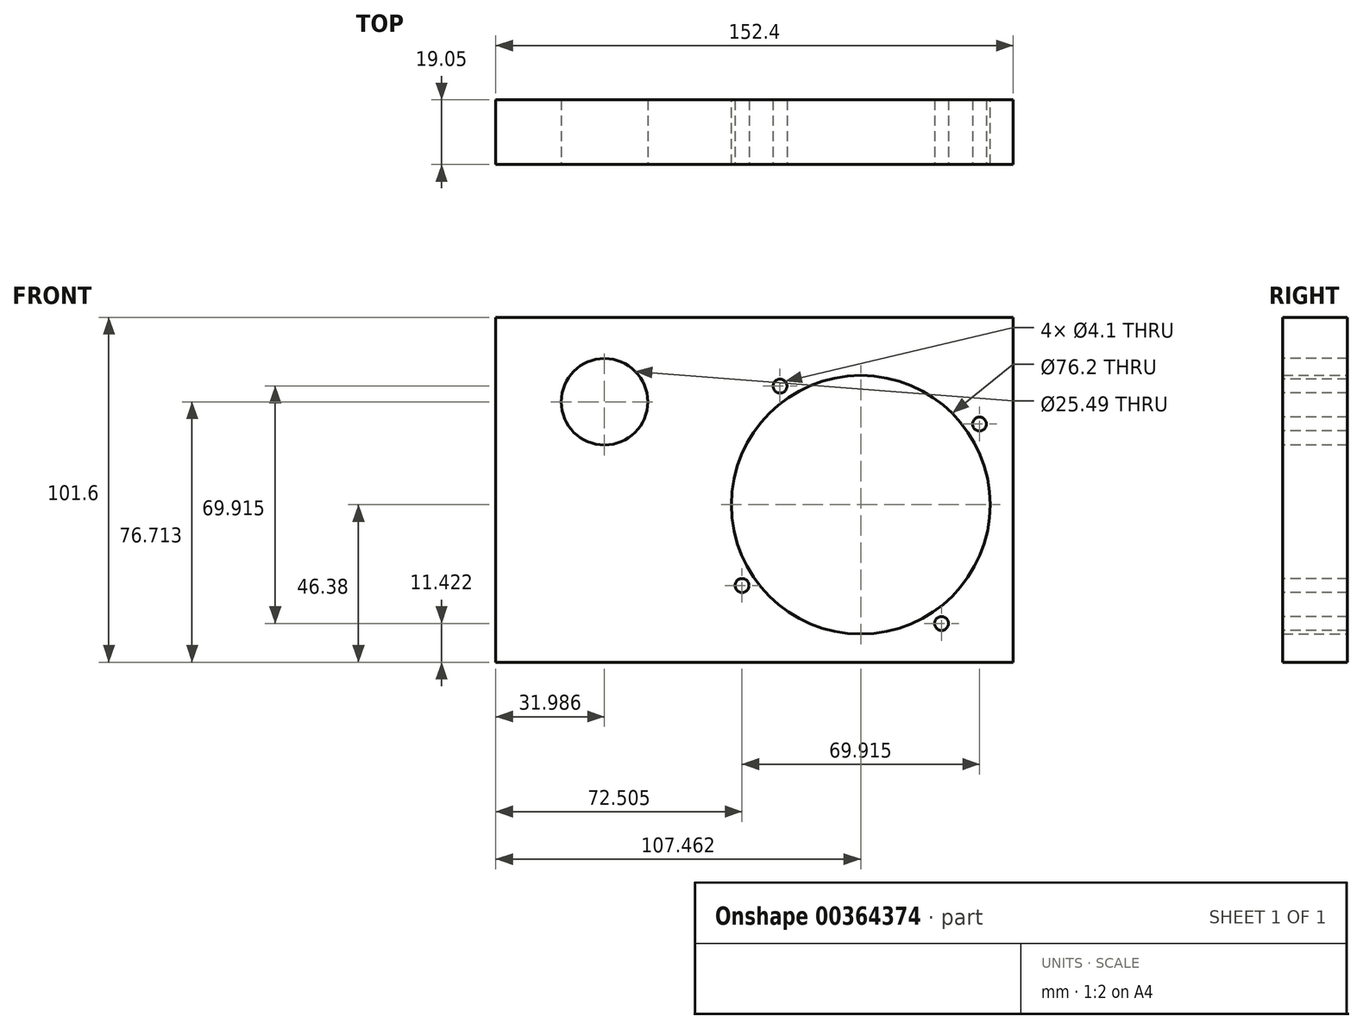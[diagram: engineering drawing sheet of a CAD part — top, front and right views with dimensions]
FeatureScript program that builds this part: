
annotation { "Feature Type Name" : "Feature", "Feature Type Description" : "" }
export const myFeature = defineFeature(function(context is Context, id is Id, definition is map)
    precondition{}
    {
        {
            var Q0;
            Q0=qCreatedBy(makeId("Front.planeOp"),FACE);
            var sketch = newSketch(context, id + "F0", { "sketchPlane" : qUnion([Q0])});
            skLineSegment(sketch, "E0.bottom", {"start": v(-73.83, 39.08) * mm, "end": v(78.57, 39.08) * mm});
            skLineSegment(sketch, "E0.top", {"start": v(-73.83, -62.52) * mm, "end": v(78.57, -62.52) * mm});
            skLineSegment(sketch, "E0.left", {"start": v(-73.83, 39.08) * mm, "end": v(-73.83, -62.52) * mm});
            skLineSegment(sketch, "E0.right", {"start": v(78.57, 39.08) * mm, "end": v(78.57, -62.52) * mm});
            skCircle(sketch, "E1", {"center": v(33.63, -16.14) * mm, "radius": 38.1 * mm});
            skSolve(sketch);
        }
        {
            var Q0;
            Q0 = qSketchRegion(id + "F0", true);
            extrude(context, id + "F1", {"entities" : qUnion([Q0]), "depth" : 19.05 * mm});
        }
        {
            var Q0;
            Q0=makeQuery(id+"F1.opExtrude","CAP_FACE",FACE,{"disambiguationData":[OSD([sQuery(id+"F0.wireOp",EDGE,"E0.bottom"),sQuery(id+"F0.wireOp",EDGE,"E0.top"),sQuery(id+"F0.wireOp",EDGE,"E0.left"),sQuery(id+"F0.wireOp",EDGE,"E0.right"),sQuery(id+"F0.wireOp",EDGE,"E1")])],"isStart":false});
            var sketch = newSketch(context, id + "F2", { "sketchPlane" : qUnion([Q0])});
            skCircle(sketch, "E2", {"center": v(-41.84, 14.2) * mm, "radius": 12.74 * mm});
            skSolve(sketch);
        }
        {
            var Q0;
            Q0 = qSketchRegion(id + "F2", true);
            extrude(context, id + "F3", {"entities" : qUnion([Q0]), "operationType" : NewBodyOperationType.REMOVE, "oppositeDirection" : true, "depth" : 25.4 * mm});
        }
        {
            var Q0;
            Q0=makeQuery(id+"F1.opExtrude","CAP_FACE",FACE,{"disambiguationData":[OSD([sQuery(id+"F0.wireOp",EDGE,"E0.bottom"),sQuery(id+"F0.wireOp",EDGE,"E0.top"),sQuery(id+"F0.wireOp",EDGE,"E0.left"),sQuery(id+"F0.wireOp",EDGE,"E0.right"),sQuery(id+"F0.wireOp",EDGE,"E1")])],"isStart":false});
            var sketch = newSketch(context, id + "F4", { "sketchPlane" : qUnion([Q0])});
            skCircle(sketch, "E3", {"center": v(33.63, -16.14) * mm, "radius": 42.28 * mm, "construction": true});
            skCircle(sketch, "E4", {"center": v(9.86, 18.82) * mm, "radius": 2.05 * mm});
            skCircle(sketch, "E5.1.0", {"center": v(-1.33, -39.92) * mm, "radius": 2.05 * mm});
            skCircle(sketch, "E5.2.0", {"center": v(57.4, -51.1) * mm, "radius": 2.05 * mm});
            skCircle(sketch, "E5.3.0", {"center": v(68.6, 7.64) * mm, "radius": 2.05 * mm});
            skSolve(sketch);
        }
        {
            var Q0;
            Q0 = qSketchRegion(id + "F4", true);
            extrude(context, id + "F5", {"entities" : qUnion([Q0]), "operationType" : NewBodyOperationType.REMOVE, "oppositeDirection" : true, "depth" : 25.4 * mm});
        }
    });
